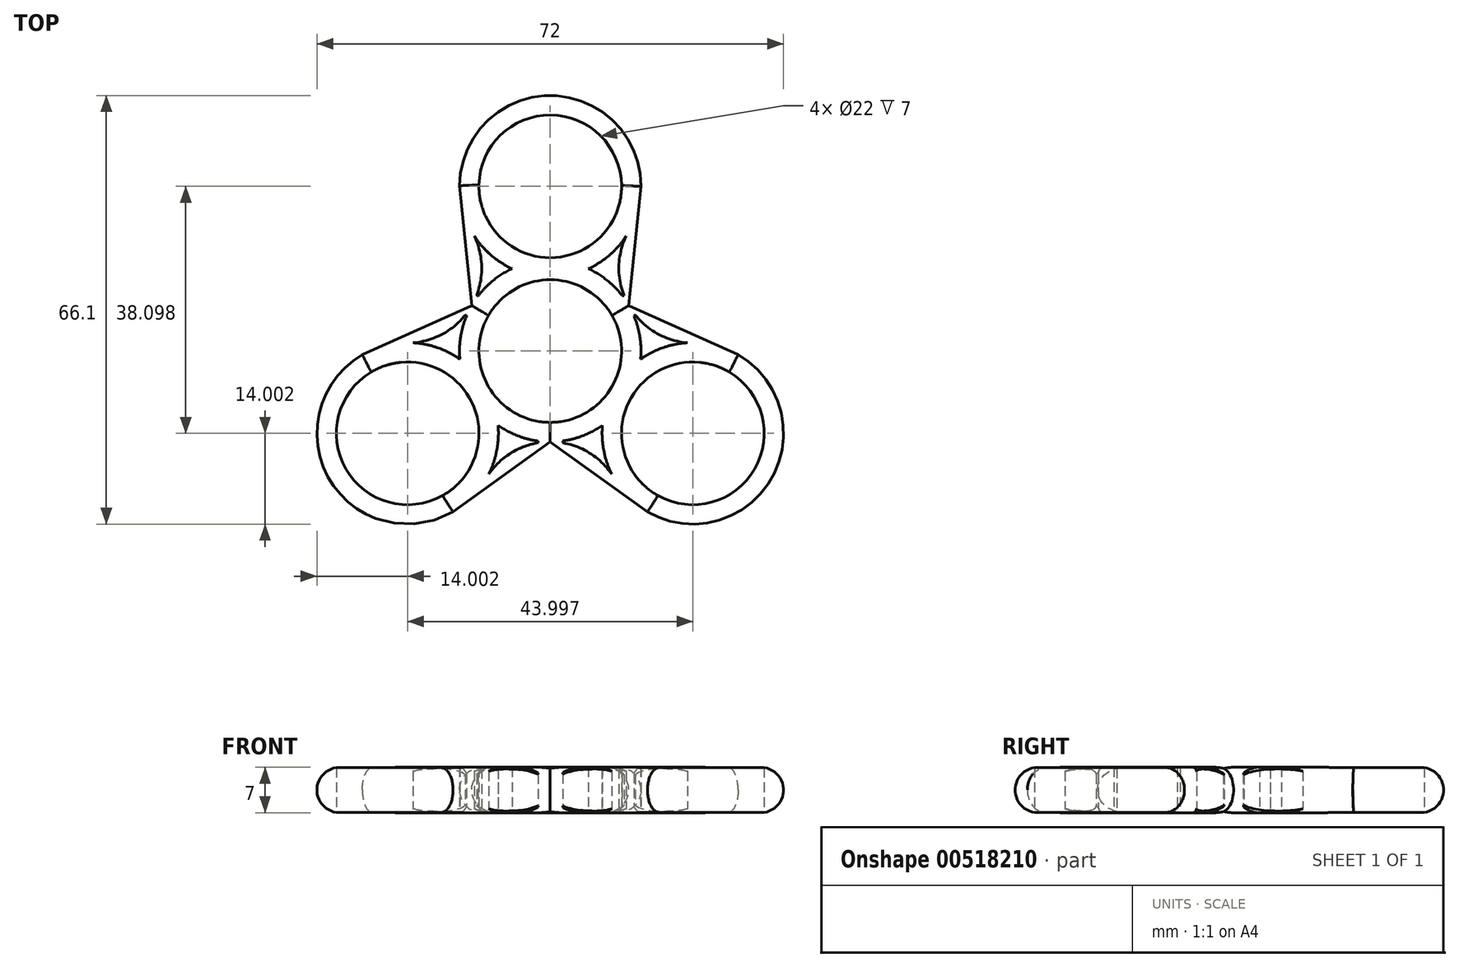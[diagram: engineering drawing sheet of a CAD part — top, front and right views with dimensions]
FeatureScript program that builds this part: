
annotation { "Feature Type Name" : "Feature", "Feature Type Description" : "" }
export const myFeature = defineFeature(function(context is Context, id is Id, definition is map)
    precondition{}
    {
        {
            var Q0;
            Q0=qCreatedBy(makeId("Top.planeOp"),FACE);
            var sketch = newSketch(context, id + "F0", { "sketchPlane" : qUnion([Q0])});
            skCircle(sketch, "E0", {"center": v(0, 0) * mm, "radius": 11 * mm});
            skArc(sketch, "E1", {"start": v(-5.9, 12.7) * mm, "mid": v(-8.77, 10.91) * mm, "end": v(-11.13, 8.49) * mm});
            skCircle(sketch, "E2", {"center": v(0, 25.4) * mm, "radius": 11 * mm});
            skArc(sketch, "E3", {"start": v(5.9, 12.7) * mm, "mid": v(9.14, 14.8) * mm, "end": v(11.7, 17.7) * mm});
            skCircle(sketch, "E4", {"center": v(22, -12.7) * mm, "radius": 11 * mm});
            skArc(sketch, "E5", {"start": v(8.05, -11.45) * mm, "mid": v(8.25, -15.32) * mm, "end": v(9.5, -18.99) * mm});
            skCircle(sketch, "E6", {"center": v(-22, -12.7) * mm, "radius": 11 * mm});
            skArc(sketch, "E7", {"start": v(-13.94, -1.25) * mm, "mid": v(-17.39, 0.52) * mm, "end": v(-21.19, 1.28) * mm});
            skArc(sketch, "E8.trimOffspring", {"start": v(13.94, -1.25) * mm, "mid": v(13.83, 2.15) * mm, "end": v(12.91, 5.42) * mm});
            skArc(sketch, "E9.trimOffspring", {"start": v(-8.05, -11.45) * mm, "mid": v(-5.12, -13.03) * mm, "end": v(-1.9, -13.87) * mm});
            skArc(sketch, "E10", {"start": v(11.7, 17.7) * mm, "mid": v(10.59, 13.17) * mm, "end": v(11.37, 8.56) * mm});
            skArc(sketch, "E11", {"start": v(9.5, -18.99) * mm, "mid": v(6.21, -15.82) * mm, "end": v(1.96, -14.17) * mm});
            skArc(sketch, "E12", {"start": v(-21.19, 1.28) * mm, "mid": v(-16.7, 2.58) * mm, "end": v(-13.11, 5.56) * mm});
            skLineSegment(sketch, "E13", {"start": v(14, 25.4) * mm, "end": v(12.12, 7) * mm});
            skLineSegment(sketch, "E14", {"start": v(12.12, 7) * mm, "end": v(29, -0.57) * mm});
            skLineSegment(sketch, "E15", {"start": v(-15, -24.82) * mm, "end": v(0, -14) * mm});
            skLineSegment(sketch, "E16", {"start": v(15, -24.82) * mm, "end": v(0, -14) * mm});
            skPoint(sketch, "E17.endSnap0", {"position": v(-12.12, 7) * mm});
            skLineSegment(sketch, "E18", {"start": v(-29, -0.57) * mm, "end": v(-12.12, 7) * mm});
            skLineSegment(sketch, "E19", {"start": v(-12.12, 7) * mm, "end": v(-14, 25.5) * mm});
            skArc(sketch, "E20.trimOffspring", {"start": v(-11.7, 17.7) * mm, "mid": v(-9.14, 14.8) * mm, "end": v(-5.9, 12.7) * mm});
            skPoint(sketch, "E21.orphan", {"position": v(-12.56, 19.22) * mm});
            skArc(sketch, "E22.trimOffspring", {"start": v(13.71, 22.57) * mm, "mid": v(-0.04, 39.4) * mm, "end": v(-13.7, 22.5) * mm});
            skPoint(sketch, "E23.orphan", {"position": v(12.56, 19.22) * mm});
            skPoint(sketch, "E24.orphan", {"position": v(-22.92, 1.27) * mm});
            skArc(sketch, "E25.trimOffspring", {"start": v(-26.4, 0.6) * mm, "mid": v(-34.12, -19.7) * mm, "end": v(-12.7, -23.16) * mm});
            skArc(sketch, "E26.trimOffspring", {"start": v(-9.5, -18.99) * mm, "mid": v(-8.25, -15.32) * mm, "end": v(-8.05, -11.45) * mm});
            skPoint(sketch, "E27.orphan", {"position": v(-10.36, -20.48) * mm});
            skArc(sketch, "E28.trimOffspring", {"start": v(12.7, -23.16) * mm, "mid": v(34.12, -19.7) * mm, "end": v(26.4, 0.6) * mm});
            skPoint(sketch, "E29.orphan", {"position": v(10.36, -20.48) * mm});
            skArc(sketch, "E30.trimOffspring", {"start": v(21.19, 1.28) * mm, "mid": v(17.39, 0.52) * mm, "end": v(13.94, -1.25) * mm});
            skPoint(sketch, "E31.orphan", {"position": v(22.92, 1.27) * mm});
            skLineSegment(sketch, "E32", {"start": v(12.91, 5.42) * mm, "end": v(13.1, 5.57) * mm});
            skPoint(sketch, "E33.end.orphan", {"position": v(11.37, 8.56) * mm});
            skPoint(sketch, "E33.start.orphan", {"position": v(11.08, 8.56) * mm});
            skArc(sketch, "E34.trimOffspring", {"start": v(11.08, 8.56) * mm, "mid": v(8.73, 10.94) * mm, "end": v(5.9, 12.7) * mm});
            skArc(sketch, "E35.trimOffspring", {"start": v(13.1, 5.57) * mm, "mid": v(16.7, 2.59) * mm, "end": v(21.19, 1.28) * mm});
            skLineSegment(sketch, "E36", {"start": v(11.08, 8.56) * mm, "end": v(11.37, 8.56) * mm});
            skLineSegment(sketch, "E37", {"start": v(-1.9, -13.87) * mm, "end": v(-1.9, -14.16) * mm});
            skLineSegment(sketch, "E38", {"start": v(1.96, -13.86) * mm, "end": v(1.96, -14.17) * mm});
            skArc(sketch, "E39.trimOffspring", {"start": v(1.96, -13.86) * mm, "mid": v(5.15, -13.02) * mm, "end": v(8.05, -11.45) * mm});
            skArc(sketch, "E40.trimOffspring", {"start": v(-1.9, -14.16) * mm, "mid": v(-6.18, -15.8) * mm, "end": v(-9.5, -18.99) * mm});
            skLineSegment(sketch, "E41", {"start": v(-11.35, 8.61) * mm, "end": v(-11.13, 8.49) * mm});
            skLineSegment(sketch, "E42", {"start": v(-12.9, 5.43) * mm, "end": v(-13.11, 5.56) * mm});
            skArc(sketch, "E43.trimOffspring", {"start": v(-12.9, 5.43) * mm, "mid": v(-13.83, 2.15) * mm, "end": v(-13.94, -1.25) * mm});
            skArc(sketch, "E44.trimOffspring", {"start": v(-11.35, 8.61) * mm, "mid": v(-10.59, 13.2) * mm, "end": v(-11.7, 17.7) * mm});
            skSolve(sketch);
        }
        {
            var Q0;
            Q0=makeQuery(id+"F0.imprint","IMPRINT",FACE,{"disambiguationData":[TD([[makeQuery(id+"F0.imprint","IMPRINT",EDGE,{"derivedFrom":sQuery(id+"F0.wireOp",EDGE,"E0")}),-1.0]])]});
            extrude(context, id + "F1", {"entities" : qUnion([Q0]), "depth" : 7 * mm, "offsetDistance" : 25.4 * mm});
        }
        {
            var Q0;
            Q0=makeQuery(id+"F1.opExtrude","CAP_EDGE",EDGE,{"disambiguationData":[OSD([sQuery(id+"F0.wireOp",EDGE,"E13")])],"isStart":false});
            var Q1;
            Q1=makeQuery(id+"F1.opExtrude","CAP_EDGE",EDGE,{"disambiguationData":[OSD([sQuery(id+"F0.wireOp",EDGE,"E22.trimOffspring")])],"isStart":false});
            var Q2;
            Q2=makeQuery(id+"F1.opExtrude","CAP_EDGE",EDGE,{"disambiguationData":[OSD([sQuery(id+"F0.wireOp",EDGE,"E19")])],"isStart":false});
            var Q3;
            Q3=makeQuery(id+"F1.opExtrude","CAP_EDGE",EDGE,{"disambiguationData":[OSD([sQuery(id+"F0.wireOp",EDGE,"E18")])],"isStart":false});
            var Q4;
            Q4=makeQuery(id+"F1.opExtrude","CAP_EDGE",EDGE,{"disambiguationData":[OSD([sQuery(id+"F0.wireOp",EDGE,"E25.trimOffspring")])],"isStart":false});
            var Q5;
            Q5=makeQuery(id+"F1.opExtrude","CAP_EDGE",EDGE,{"disambiguationData":[OSD([sQuery(id+"F0.wireOp",EDGE,"E15")])],"isStart":false});
            var Q6;
            Q6=makeQuery(id+"F1.opExtrude","CAP_EDGE",EDGE,{"disambiguationData":[OSD([sQuery(id+"F0.wireOp",EDGE,"E16")])],"isStart":false});
            var Q7;
            Q7=makeQuery(id+"F1.opExtrude","CAP_EDGE",EDGE,{"disambiguationData":[OSD([sQuery(id+"F0.wireOp",EDGE,"E28.trimOffspring")])],"isStart":false});
            var Q8;
            Q8=makeQuery(id+"F1.opExtrude","CAP_EDGE",EDGE,{"disambiguationData":[OSD([sQuery(id+"F0.wireOp",EDGE,"E14")])],"isStart":false});
            var Q9;
            Q9=makeQuery(id+"F1.opExtrude","CAP_EDGE",EDGE,{"disambiguationData":[OSD([sQuery(id+"F0.wireOp",EDGE,"E13")])],"isStart":true});
            var Q10;
            Q10=makeQuery(id+"F1.opExtrude","CAP_EDGE",EDGE,{"disambiguationData":[OSD([sQuery(id+"F0.wireOp",EDGE,"E14")])],"isStart":true});
            var Q11;
            Q11=makeQuery(id+"F1.opExtrude","CAP_EDGE",EDGE,{"disambiguationData":[OSD([sQuery(id+"F0.wireOp",EDGE,"E19")])],"isStart":true});
            var Q12;
            Q12=makeQuery(id+"F1.opExtrude","CAP_EDGE",EDGE,{"disambiguationData":[OSD([sQuery(id+"F0.wireOp",EDGE,"E22.trimOffspring")])],"isStart":true});
            var Q13;
            Q13=makeQuery(id+"F1.opExtrude","CAP_EDGE",EDGE,{"disambiguationData":[OSD([sQuery(id+"F0.wireOp",EDGE,"E18")])],"isStart":true});
            var Q14;
            Q14=makeQuery(id+"F1.opExtrude","CAP_EDGE",EDGE,{"disambiguationData":[OSD([sQuery(id+"F0.wireOp",EDGE,"E25.trimOffspring")])],"isStart":true});
            var Q15;
            Q15=makeQuery(id+"F1.opExtrude","CAP_EDGE",EDGE,{"disambiguationData":[OSD([sQuery(id+"F0.wireOp",EDGE,"E15")])],"isStart":true});
            var Q16;
            Q16=makeQuery(id+"F1.opExtrude","CAP_EDGE",EDGE,{"disambiguationData":[OSD([sQuery(id+"F0.wireOp",EDGE,"E16")])],"isStart":true});
            var Q17;
            Q17=makeQuery(id+"F1.opExtrude","CAP_EDGE",EDGE,{"disambiguationData":[OSD([sQuery(id+"F0.wireOp",EDGE,"E28.trimOffspring")])],"isStart":true});
            fillet(context, id + "F2", {"entities" : qUnion([Q0, Q1, Q2, Q3, Q4, Q5, Q6, Q7, Q8, Q9, Q10, Q11, Q12, Q13, Q14, Q15, Q16, Q17]), "radius" : 3.5 * mm, "tangentPropagation" : true, "allowEdgeOverflow" : false});
        }
    });
